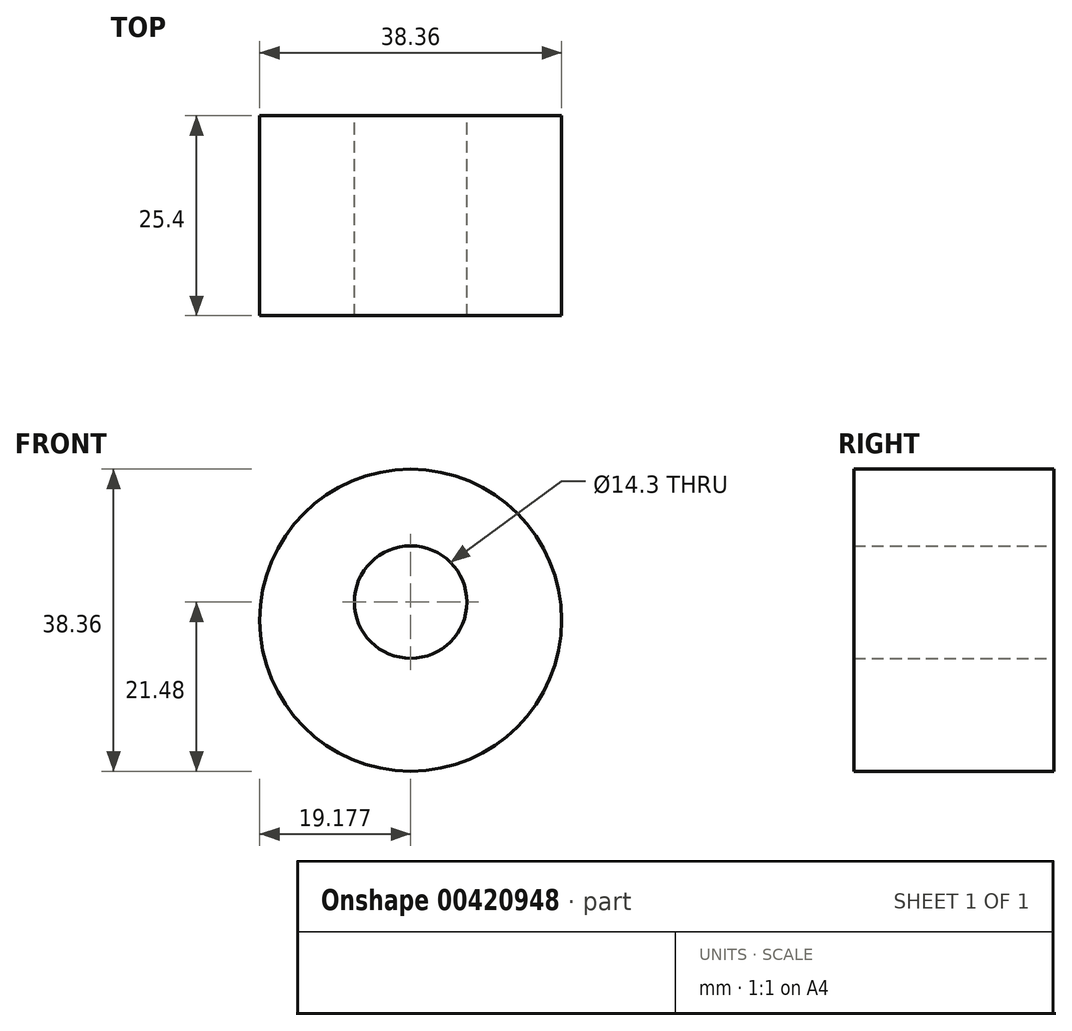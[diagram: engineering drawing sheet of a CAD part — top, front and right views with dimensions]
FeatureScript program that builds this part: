
annotation { "Feature Type Name" : "Feature", "Feature Type Description" : "" }
export const myFeature = defineFeature(function(context is Context, id is Id, definition is map)
    precondition{}
    {
        {
            var Q0;
            Q0=qCreatedBy(makeId("Front.planeOp"),FACE);
            var sketch = newSketch(context, id + "F0", { "sketchPlane" : qUnion([Q0])});
            skCircle(sketch, "E0", {"center": v(-19.28, -19.28) * mm, "radius": 19.18 * mm});
            skCircle(sketch, "E1", {"center": v(-19.28, -16.98) * mm, "radius": 12.39 * mm});
            skCircle(sketch, "E2", {"center": v(-19.28, -16.98) * mm, "radius": 7.15 * mm});
            skSolve(sketch);
        }
        {
            var Q0;
            Q0 = qSketchRegion(id + "F0", true);
            var Q1;
            Q1=makeQuery(id+"F0.imprint","IMPRINT",FACE,{"disambiguationData":[TD([[makeQuery(id+"F0.imprint","IMPRINT",EDGE,{"derivedFrom":sQuery(id+"F0.wireOp",EDGE,"E1")}),1.0]])]});
            extrude(context, id + "F1", {"entities" : qUnion([Q0, Q1]), "depth" : 25.4 * mm});
        }
    });
